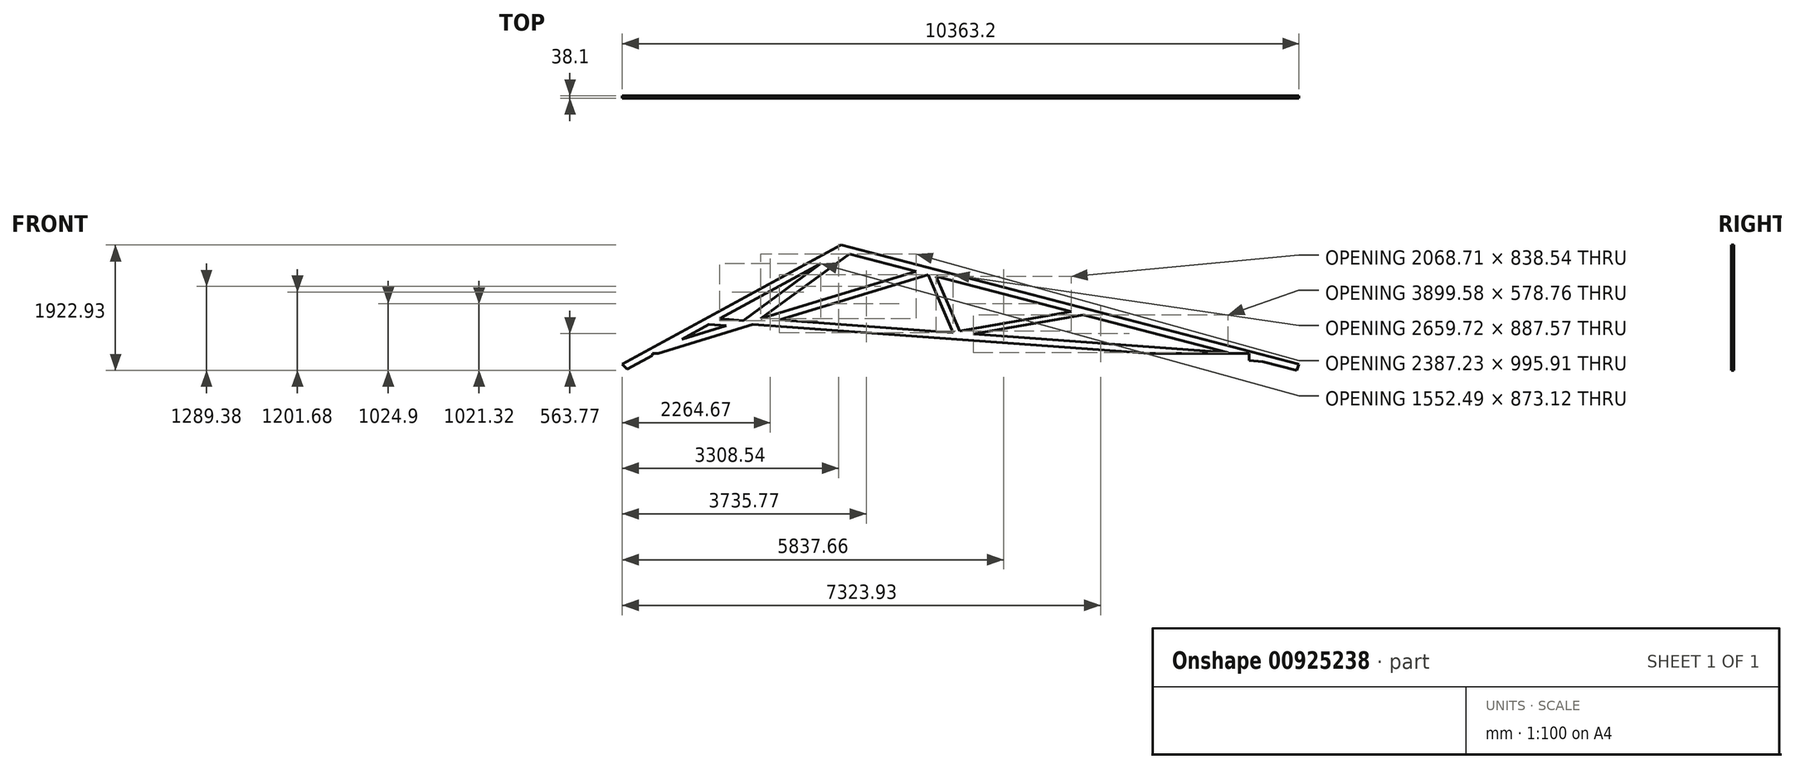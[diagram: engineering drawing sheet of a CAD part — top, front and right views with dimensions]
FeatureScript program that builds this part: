
annotation { "Feature Type Name" : "Feature", "Feature Type Description" : "" }
export const myFeature = defineFeature(function(context is Context, id is Id, definition is map)
    precondition{}
    {
        {
            var Q0;
            Q0=qCreatedBy(makeId("Front.planeOp"),FACE);
            var sketch = newSketch(context, id + "F0", { "sketchPlane" : qUnion([Q0])});
            skLineSegment(sketch, "E0", {"start": v(0, 0) * mm, "end": v(3352.8, 1828.8) * mm});
            skLineSegment(sketch, "E1", {"start": v(3352.8, 1828.8) * mm, "end": v(10363.2, 0) * mm});
            skLineSegment(sketch, "E2", {"start": v(10363.2, 0) * mm, "end": v(9599.5, 55.66) * mm});
            skLineSegment(sketch, "E3", {"start": v(913.2, 383.54) * mm, "end": v(1325.33, 608.33) * mm});
            skLineSegment(sketch, "E4", {"start": v(1325.33, 608.33) * mm, "end": v(1587.85, 589.2) * mm});
            skLineSegment(sketch, "E5", {"start": v(1587.85, 589.2) * mm, "end": v(913.2, 383.54) * mm});
            skLineSegment(sketch, "E6", {"start": v(1488.42, 697.3) * mm, "end": v(3040.92, 1544.1) * mm});
            skLineSegment(sketch, "E7", {"start": v(3040.92, 1544.1) * mm, "end": v(1849.3, 671) * mm});
            skLineSegment(sketch, "E8", {"start": v(1849.3, 671) * mm, "end": v(1488.42, 697.3) * mm});
            skLineSegment(sketch, "E9", {"start": v(2114.92, 697.3) * mm, "end": v(3474.13, 1693.2) * mm});
            skLineSegment(sketch, "E10", {"start": v(3474.13, 1693.2) * mm, "end": v(4502.15, 1425.02) * mm});
            skLineSegment(sketch, "E11", {"start": v(4502.15, 1425.02) * mm, "end": v(2114.92, 697.3) * mm});
            skLineSegment(sketch, "E12", {"start": v(2405.91, 680.84) * mm, "end": v(4681.55, 1374.55) * mm});
            skLineSegment(sketch, "E13", {"start": v(4681.55, 1374.55) * mm, "end": v(5065.63, 486.98) * mm});
            skLineSegment(sketch, "E14", {"start": v(5065.63, 486.98) * mm, "end": v(2405.91, 680.84) * mm});
            skLineSegment(sketch, "E15", {"start": v(4803.3, 1346.46) * mm, "end": v(5166.17, 507.92) * mm});
            skLineSegment(sketch, "E16", {"start": v(5166.17, 507.92) * mm, "end": v(6872.01, 806.8) * mm});
            skLineSegment(sketch, "E17", {"start": v(6872.01, 806.8) * mm, "end": v(4803.3, 1346.46) * mm});
            skLineSegment(sketch, "E18", {"start": v(5374.14, 464.5) * mm, "end": v(7055.15, 759.02) * mm});
            skLineSegment(sketch, "E19", {"start": v(7055.15, 759.02) * mm, "end": v(9273.72, 180.26) * mm});
            skLineSegment(sketch, "E20", {"start": v(9273.72, 180.26) * mm, "end": v(5374.14, 464.5) * mm});
            skPoint(sketch, "E21.start.orphan", {"position": v(1999.73, 609.6) * mm});
            skPoint(sketch, "E22.end.orphan", {"position": v(6858, 914.4) * mm});
            skLineSegment(sketch, "E23.top", {"start": v(9599.5, 166.95) * mm, "end": v(8072.7, 166.95) * mm});
            skLineSegment(sketch, "E23.left", {"start": v(9599.5, 166.95) * mm, "end": v(9599.5, 55.66) * mm});
            skLineSegment(sketch, "E23.right", {"start": v(458.06, 166.95) * mm, "end": v(458.06, 135.27) * mm});
            skLineSegment(sketch, "E24.trimOffspring", {"start": v(547.67, 166.95) * mm, "end": v(458.06, 166.95) * mm});
            skLineSegment(sketch, "E25.trimOffspring", {"start": v(8072.7, 166.95) * mm, "end": v(1999.73, 609.6) * mm});
            skLineSegment(sketch, "E26.trimOffspring", {"start": v(547.67, 166.95) * mm, "end": v(1999.73, 609.6) * mm});
            skLineSegment(sketch, "E27", {"start": v(73.06, -74.73) * mm, "end": v(458.06, 135.27) * mm});
            skLineSegment(sketch, "E28", {"start": v(0, 0) * mm, "end": v(73.06, -74.73) * mm});
            skLineSegment(sketch, "E29", {"start": v(10325.57, -94.13) * mm, "end": v(10363.2, 0) * mm});
            skLineSegment(sketch, "E30.trimOffspring", {"start": v(9810.22, 40.3) * mm, "end": v(10325.57, -94.13) * mm});
            skSolve(sketch);
        }
        {
            var Q0;
            Q0 = qSketchRegion(id + "F0", true);
            extrude(context, id + "F1", {"entities" : qUnion([Q0]), "depth" : 38.1 * mm, "offsetDistance" : 30.48 * mm});
        }
    });
